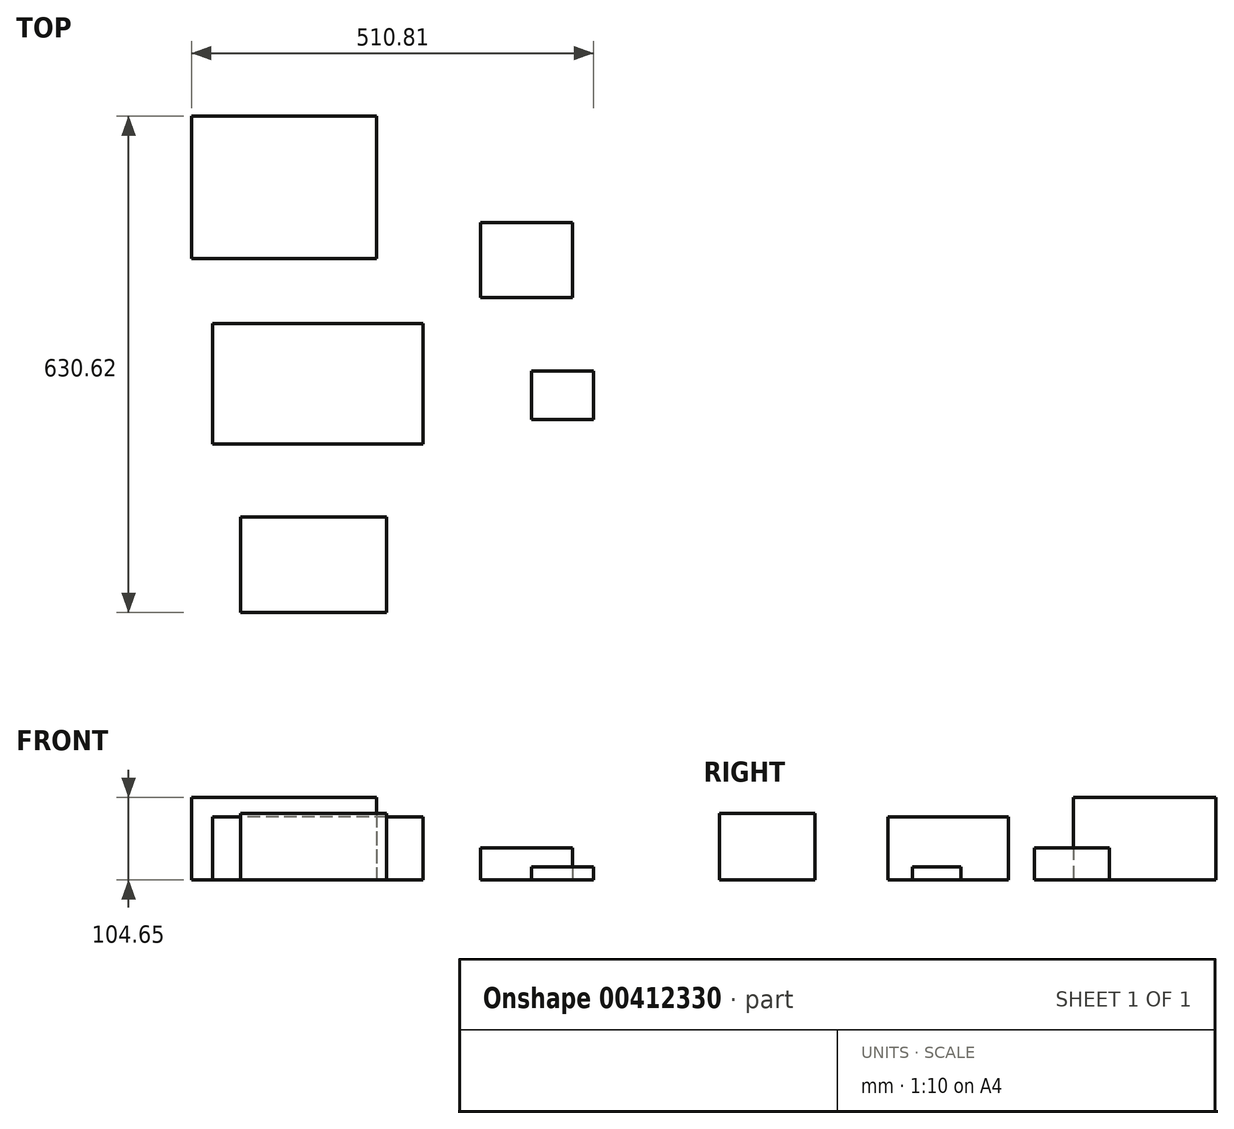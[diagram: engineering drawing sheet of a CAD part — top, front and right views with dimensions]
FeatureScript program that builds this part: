
annotation { "Feature Type Name" : "Feature", "Feature Type Description" : "" }
export const myFeature = defineFeature(function(context is Context, id is Id, definition is map)
    precondition{}
    {
        {
            var Q0;
            Q0=qCreatedBy(makeId("Top.planeOp"),FACE);
            var sketch = newSketch(context, id + "F0", { "sketchPlane" : qUnion([Q0])});
            skLineSegment(sketch, "E0.bottom", {"start": v(133.86, 76.7) * mm, "end": v(-133.86, 76.7) * mm});
            skLineSegment(sketch, "E0.top", {"start": v(133.86, -76.7) * mm, "end": v(-133.86, -76.7) * mm});
            skLineSegment(sketch, "E0.left", {"start": v(133.86, 76.7) * mm, "end": v(133.86, -76.7) * mm});
            skLineSegment(sketch, "E0.right", {"start": v(-133.86, 76.7) * mm, "end": v(-133.86, -76.7) * mm});
            skPoint(sketch, "E0.middle", {"position": v(0, 0) * mm});
            skSolve(sketch);
        }
        {
            var Q0;
            Q0=makeQuery(id+"F0.imprint","IMPRINT",FACE,{"disambiguationData":[TD([[makeQuery(id+"F0.imprint","IMPRINT",EDGE,{"derivedFrom":sQuery(id+"F0.wireOp",EDGE,"E0.bottom")}),1.0]])]});
            extrude(context, id + "F1", {"entities" : qUnion([Q0]), "depth" : 80.26 * mm});
        }
        {
            var Q0;
            Q0=qCreatedBy(makeId("Top.planeOp"),FACE);
            var sketch = newSketch(context, id + "F2", { "sketchPlane" : qUnion([Q0])});
            skLineSegment(sketch, "E1.bottom", {"start": v(-98.07, -169.04) * mm, "end": v(87.1, -169.04) * mm});
            skLineSegment(sketch, "E1.top", {"start": v(-98.07, -290.45) * mm, "end": v(87.1, -290.45) * mm});
            skLineSegment(sketch, "E1.left", {"start": v(-98.07, -169.04) * mm, "end": v(-98.07, -290.45) * mm});
            skLineSegment(sketch, "E1.right", {"start": v(87.1, -169.04) * mm, "end": v(87.1, -290.45) * mm});
            skSolve(sketch);
        }
        {
            var Q0;
            Q0=makeQuery(id+"F2.imprint","IMPRINT",FACE,{"disambiguationData":[TD([[makeQuery(id+"F2.imprint","IMPRINT",EDGE,{"derivedFrom":sQuery(id+"F2.wireOp",EDGE,"E1.bottom")}),-1.0]])]});
            extrude(context, id + "F3", {"entities" : qUnion([Q0]), "depth" : 84.58 * mm});
        }
        {
            var Q0;
            Q0=qCreatedBy(makeId("Top.planeOp"),FACE);
            var sketch = newSketch(context, id + "F4", { "sketchPlane" : qUnion([Q0])});
            skLineSegment(sketch, "E2.bottom", {"start": v(74.43, 159.32) * mm, "end": v(-160.52, 159.32) * mm});
            skLineSegment(sketch, "E2.top", {"start": v(74.43, 340.17) * mm, "end": v(-160.52, 340.17) * mm});
            skLineSegment(sketch, "E2.left", {"start": v(74.43, 159.32) * mm, "end": v(74.43, 340.17) * mm});
            skLineSegment(sketch, "E2.right", {"start": v(-160.52, 159.32) * mm, "end": v(-160.52, 340.17) * mm});
            skSolve(sketch);
        }
        {
            var Q0;
            Q0=makeQuery(id+"F4.imprint","IMPRINT",FACE,{"disambiguationData":[TD([[makeQuery(id+"F4.imprint","IMPRINT",EDGE,{"derivedFrom":sQuery(id+"F4.wireOp",EDGE,"E2.bottom")}),-1.0]])]});
            extrude(context, id + "F5", {"entities" : qUnion([Q0]), "depth" : 104.65 * mm});
        }
        {
            var Q0;
            Q0=qCreatedBy(makeId("Top.planeOp"),FACE);
            var sketch = newSketch(context, id + "F6", { "sketchPlane" : qUnion([Q0])});
            skLineSegment(sketch, "E3.bottom", {"start": v(350.29, 16.44) * mm, "end": v(271.29, 16.44) * mm});
            skLineSegment(sketch, "E3.top", {"start": v(350.29, -45.56) * mm, "end": v(271.29, -45.56) * mm});
            skLineSegment(sketch, "E3.left", {"start": v(350.29, 16.44) * mm, "end": v(350.29, -45.56) * mm});
            skLineSegment(sketch, "E3.right", {"start": v(271.29, 16.44) * mm, "end": v(271.29, -45.56) * mm});
            skSolve(sketch);
        }
        {
            var Q0;
            Q0=makeQuery(id+"F6.imprint","IMPRINT",FACE,{"disambiguationData":[TD([[makeQuery(id+"F6.imprint","IMPRINT",EDGE,{"derivedFrom":sQuery(id+"F6.wireOp",EDGE,"E3.bottom")}),1.0]])]});
            extrude(context, id + "F7", {"entities" : qUnion([Q0]), "depth" : 16.5 * mm});
        }
        {
            var Q0;
            Q0=qCreatedBy(makeId("Top.planeOp"),FACE);
            var sketch = newSketch(context, id + "F8", { "sketchPlane" : qUnion([Q0])});
            skLineSegment(sketch, "E4.bottom", {"start": v(323.49, 204.93) * mm, "end": v(206.65, 204.93) * mm});
            skLineSegment(sketch, "E4.top", {"start": v(323.49, 109.68) * mm, "end": v(206.65, 109.68) * mm});
            skLineSegment(sketch, "E4.left", {"start": v(323.49, 204.93) * mm, "end": v(323.49, 109.68) * mm});
            skLineSegment(sketch, "E4.right", {"start": v(206.65, 204.93) * mm, "end": v(206.65, 109.68) * mm});
            skSolve(sketch);
        }
        {
            var Q0;
            Q0=makeQuery(id+"F8.imprint","IMPRINT",FACE,{"disambiguationData":[TD([[makeQuery(id+"F8.imprint","IMPRINT",EDGE,{"derivedFrom":sQuery(id+"F8.wireOp",EDGE,"E4.bottom")}),1.0]])]});
            extrude(context, id + "F9", {"entities" : qUnion([Q0]), "depth" : 40.64 * mm});
        }
    });
